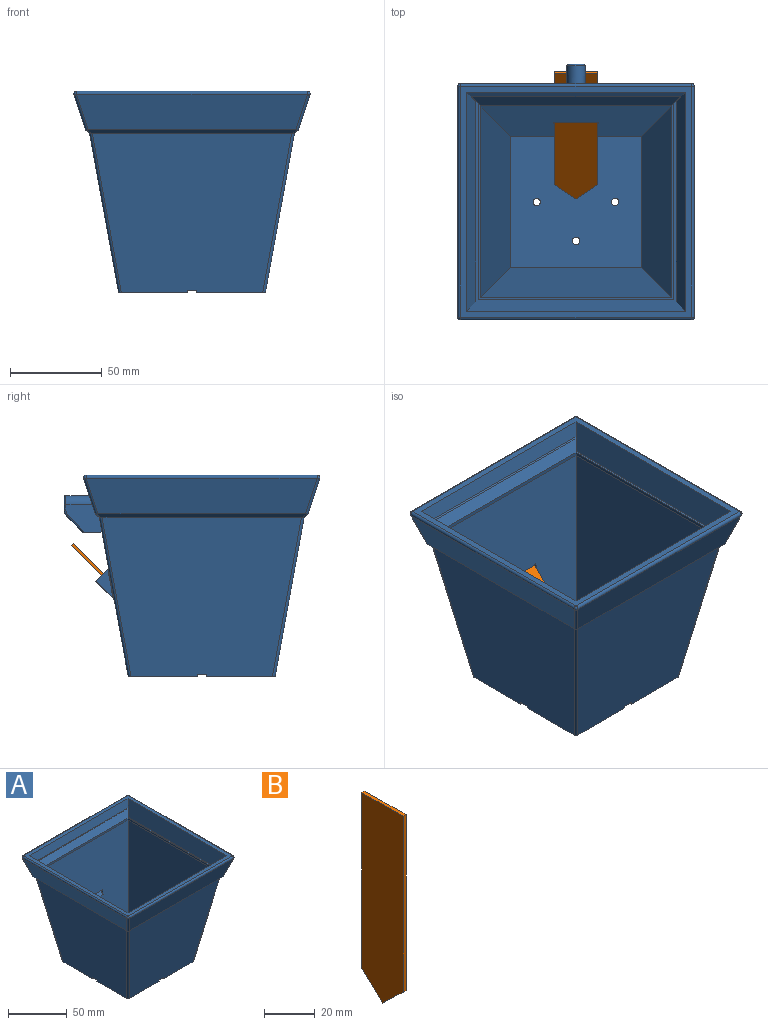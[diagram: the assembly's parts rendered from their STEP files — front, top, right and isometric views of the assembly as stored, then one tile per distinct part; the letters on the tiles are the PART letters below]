
ASSEMBLY  parts=2 mates=1
PART A: 106 faces, bbox 128.8x139.8x110.1 mm
  f0: plane 19.66x15mm, normal (1,0,0), area 207.3mm2, adj f2,f3,f19,f73,f74,f99,f100,f103
  f1: plane 19.66x15mm, normal (-1,0,0), area 207.3mm2, adj f2,f19,f47,f73,f74,f96,f97,f105
  f2: plane 108.7x87.05mm, normal (0,0.98,-0.18), area 7581.6mm2, adj f0,f1,f3,f8,f16,f44,f47,f49
  f3: plane 51.94x2.23mm, normal (0,0.64,-0.77), area 142.9mm2, adj f0,f2,f19,f53,f56,f60
  f4: plane 37.5x37.5mm, normal (0,0,-1), area 1405.8mm2, adj f5,f7,f11,f51,f72
  f5: plane 108.7x87.05mm, normal (0,-0.98,-0.18), area 8209.6mm2, adj f4,f10,f44,f46,f51,f66,f71,f72
  f6: plane 37.77x1.5mm, normal (0,1,0), area 56.5mm2, adj f10,f15,f44,f71
  f7: plane 37.77x1.5mm, normal (0,1,0), area 56.5mm2, adj f4,f11,f44,f72
  f8: plane 37.5x37.5mm, normal (0,0,-1), area 1405.8mm2, adj f2,f9,f15,f53,f69
  f9: plane 37.77x1.5mm, normal (0,-1,0), area 56.5mm2, adj f8,f15,f44,f69
  f10: plane 37.5x37.5mm, normal (0,0,-1), area 1405.8mm2, adj f5,f6,f15,f66,f71
  f11: plane 108.7x87.05mm, normal (-0.98,0,-0.18), area 8209.6mm2, adj f4,f7,f16,f43,f44,f48,f49,f51
  f12: plane 106.38x106.38mm, normal (0,0,1), area 316.1mm2, adj f27,f28,f30,f31,f32,f33,f39,f41
  f13: plane 119.46x7.5mm, normal (0,-0.95,0.31), area 924.4mm2, adj f21,f24,f25,f42
  f14: plane 113.86x6.55mm, normal (0,-0.95,0.31), area 770.8mm2, adj f22,f24,f25,f40
  f15: plane 108.7x87.05mm, normal (0.98,0,-0.18), area 8209.6mm2, adj f6,f8,f9,f10,f44,f45,f53,f66
  f16: plane 37.5x37.5mm, normal (0,0,-1), area 1405.8mm2, adj f2,f11,f43,f49,f70
  f17: plane 125.84x19.18mm, normal (0,-0.95,-0.31), area 2414.7mm2, adj f46,f57,f63,f67
  f18: plane 125.84x19.18mm, normal (0.95,0,-0.31), area 2414.7mm2, adj f45,f60,f64,f67
  f19: plane 125.84x19.18mm, normal (0,0.95,-0.31), area 2320.6mm2, adj f0,f1,f3,f47,f52,f59,f60,f73
  f20: plane 125.84x19.18mm, normal (-0.95,0,-0.31), area 2414.7mm2, adj f48,f52,f57,f58
  f21: plane 125.84x125.84mm, normal (0,0,1), area 1565mm2, adj f13,f23,f24,f25,f58,f59,f63,f64
  f22: plane 109.51x109.51mm, normal (0,0,1), area 675.3mm2, adj f14,f23,f24,f25,f29,f30,f31,f32
  f23: plane 119.46x15mm, normal (0,0.95,0.31), area 1809.4mm2, adj f21,f22,f24,f25
  f24: plane 119.46x15mm, normal (-0.95,0,0.31), area 1809.4mm2, adj f13,f14,f21,f22,f23,f41
  f25: plane 119.46x15mm, normal (0.95,0,0.31), area 1809.4mm2, adj f13,f14,f21,f22,f23,f39
  f26: plane 104.38x2mm, normal (0,-1,0), area 208.8mm2, adj f27,f33,f35,f42
  f27: plane 104.38x2mm, normal (-1,0,0), area 208.8mm2, adj f12,f26,f28,f38
  f28: plane 104.38x2mm, normal (0,1,0), area 208.8mm2, adj f12,f27,f33,f37
  f29: plane 106.38x2mm, normal (0,1,0), area 212.8mm2, adj f22,f30,f32,f40
  f30: plane 106.38x2mm, normal (-1,0,0), area 212.8mm2, adj f12,f22,f29,f31
  f31: plane 106.38x2mm, normal (0,-1,0), area 212.8mm2, adj f12,f22,f30,f32
  f32: plane 106.38x2mm, normal (1,0,0), area 212.8mm2, adj f12,f22,f29,f31
  f33: plane 104.38x2mm, normal (1,0,0), area 208.8mm2, adj f12,f26,f28,f36
  f34: plane 71.65x71.65mm, normal (0,0,1), area 5084.1mm2, adj f35,f36,f37,f38,f91,f92,f93,f94
  f35: plane 104.38x90mm, normal (0,-0.98,0.18), area 7942.5mm2, adj f26,f34,f36,f38,f80,f81,f82,f83
  f36: plane 104.38x90mm, normal (0.98,0,0.18), area 8051.5mm2, adj f33,f34,f35,f37
  f37: plane 104.38x90mm, normal (0,0.98,0.18), area 8051.5mm2, adj f28,f34,f36,f38
  f38: plane 104.38x90mm, normal (-0.98,0,0.18), area 8051.5mm2, adj f27,f34,f35,f37
  f39: plane 5.5x5.05mm, normal (-0.71,-0.71,0), area 5.4mm2, adj f12,f25,f40,f42
  f40: plane 113.86x4.55mm, normal (0,0.77,-0.63), area 648.5mm2, adj f14,f29,f39,f41
  f41: plane 5.5x5.05mm, normal (0.71,-0.71,0), area 5.4mm2, adj f12,f24,f40,f42
  f42: plane 114.49x5.5mm, normal (0,-0.74,0.68), area 817.3mm2, adj f13,f26,f39,f41
  f43: plane 37.77x1.5mm, normal (0,-1,0), area 56.5mm2, adj f11,f16,f44,f70
  f44: plane 80.55x80.55mm, normal (0,0,-1), area 730.2mm2, adj f2,f5,f6,f7,f9,f11,f15,f43
  f45: plane 113.89x2.23mm, normal (0.64,0,-0.77), area 313.9mm2, adj f15,f18,f53,f56,f60,f66,f67,f68
  f46: plane 113.89x2.23mm, normal (0,-0.64,-0.77), area 313.9mm2, adj f5,f17,f51,f54,f57,f66,f67,f68
  f47: plane 51.94x2.23mm, normal (0,0.64,-0.77), area 142.9mm2, adj f1,f2,f19,f49,f50,f52
  f48: plane 113.89x2.23mm, normal (-0.64,0,-0.77), area 313.9mm2, adj f11,f20,f49,f50,f51,f52,f54,f57
  f49: cylinder r=1.5mm len=87.17mm, axis (0.18,-0.18,-0.97), area 207.2mm2, adj f2,f11,f16,f47,f48,f50
  f50: cylinder r=1.5mm len=3.15mm, axis (-0.61,0.61,0.51), area 5mm2, adj f47,f48,f49,f52
  f51: cylinder r=1.5mm len=87.17mm, axis (-0.18,-0.18,0.97), area 207.2mm2, adj f4,f5,f11,f46,f48,f54
  f52: cylinder r=1.5mm len=19.36mm, axis (-0.3,0.3,0.91), area 46.7mm2, adj f19,f20,f47,f48,f50,f55
  f53: cylinder r=1.5mm len=87.17mm, axis (0.18,0.18,0.97), area 207.2mm2, adj f2,f3,f8,f15,f45,f56
  f54: cylinder r=1.5mm len=3.15mm, axis (-0.61,-0.61,0.51), area 5mm2, adj f46,f48,f51,f57
  f55: sphere r=1.5mm, area 4.9mm2, adj f52,f58,f59
  f56: cylinder r=1.5mm len=3.15mm, axis (-0.61,-0.61,-0.51), area 5mm2, adj f3,f45,f53,f60
  f57: cylinder r=1.5mm len=19.36mm, axis (-0.3,-0.3,0.91), area 46.7mm2, adj f17,f20,f46,f48,f54,f61
  f58: cylinder r=1.5mm len=125.84mm, axis (0,-1,0), area 357mm2, adj f20,f21,f55,f61
  f59: cylinder r=1.5mm len=125.84mm, axis (-1,0,0), area 357mm2, adj f19,f21,f55,f62
  f60: cylinder r=1.5mm len=19.36mm, axis (0.3,0.3,0.91), area 46.7mm2, adj f3,f18,f19,f45,f56,f62
  f61: sphere r=1.5mm, area 4.9mm2, adj f57,f58,f63
  f62: sphere r=1.5mm, area 4.9mm2, adj f59,f60,f64
  f63: cylinder r=1.5mm len=125.84mm, axis (1,0,0), area 357mm2, adj f17,f21,f61,f65
  f64: cylinder r=1.5mm len=125.84mm, axis (0,1,0), area 357mm2, adj f18,f21,f62,f65
  f65: sphere r=1.5mm, area 4.9mm2, adj f63,f64,f67
  f66: cylinder r=1.5mm len=87.17mm, axis (-0.18,0.18,-0.97), area 207.2mm2, adj f5,f10,f15,f45,f46,f68
  f67: cylinder r=1.5mm len=19.36mm, axis (0.3,-0.3,0.91), area 46.7mm2, adj f17,f18,f45,f46,f65,f68
  f68: cylinder r=1.5mm len=3.15mm, axis (-0.61,0.61,-0.51), area 5mm2, adj f45,f46,f66,f67
  f69: plane 37.77x1.5mm, normal (-1,0,0), area 56.5mm2, adj f2,f8,f9,f44
  f70: plane 37.77x1.5mm, normal (1,0,0), area 56.5mm2, adj f2,f16,f43,f44
  f71: plane 37.77x1.5mm, normal (-1,0,0), area 56.5mm2, adj f5,f6,f10,f44
  f72: plane 37.77x1.5mm, normal (1,0,0), area 56.5mm2, adj f4,f5,f7,f44
  f73: cylinder r=5mm len=14.36mm, axis (0,1,0), area 209mm2, adj f0,f1,f19,f98
  f74: plane 10.66x10mm, normal (0,0,-1), area 106mm2, adj f0,f1,f2,f95,f96,f100
  f75: plane 8x6.93mm, normal (0,1,0), area 36mm2, adj f97,f98,f99,f101,f104
  f76: plane 15.25x9.03mm, normal (-1,0,0), area 56.4mm2, adj f79,f84,f85
  f77: plane 29x10.04mm, normal (0,0.7,-0.71), area 409.6mm2, adj f79,f84,f87,f90
  f78: plane 15.25x9.03mm, normal (1,0,0), area 56.4mm2, adj f79,f86,f87
  f79: plane 31x7.11mm, normal (0,0.71,0.7), area 237.5mm2, adj f2,f76,f77,f78,f80,f81,f82,f83
  f80: plane 25x10mm, normal (0,0.7,-0.71), area 351.8mm2, adj f35,f79,f81,f82
  f81: plane 14.19x12.54mm, normal (1,0,0), area 39.6mm2, adj f35,f79,f80,f83
  f82: plane 14.19x12.54mm, normal (-1,0,0), area 39.6mm2, adj f35,f79,f80,f83
  f83: plane 25x12.54mm, normal (0,-0.7,0.71), area 441.1mm2, adj f35,f79,f81,f82
  f84: cylinder r=0.5mm len=10.39mm, axis (0,-0.71,-0.7), area 10.7mm2, adj f76,f77,f79,f88
  f85: cylinder r=0.5mm len=15.68mm, axis (0,0.18,0.98), area 12.3mm2, adj f2,f76,f79,f88
  f86: cylinder r=0.5mm len=15.68mm, axis (0,-0.18,-0.98), area 12.3mm2, adj f2,f78,f79,f89
  f87: cylinder r=0.5mm len=10.39mm, axis (0,0.71,0.7), area 10.7mm2, adj f77,f78,f79,f89
  f88: bspline ~1.72x1mm, area 1mm2, adj f2,f84,f85,f90
  f89: bspline ~1.72x1mm, area 1mm2, adj f2,f86,f87,f90
  f90: cylinder r=0.5mm len=29mm, axis (-1,0,0), area 8.9mm2, adj f2,f77,f88,f89
  f91: cylinder r=2mm len=4mm, axis (0,0,-1), area 44mm2, adj f34,f44
  f92: cylinder r=2mm len=4mm, axis (0,0,-1), area 44mm2, adj f34,f44
  f93: cylinder r=2mm len=4mm, axis (0,0,-1), area 44mm2, adj f34,f44
  f94: cylinder r=2mm len=4mm, axis (0,0,-1), area 44mm2, adj f34,f44
  f95: plane 8.54x8.54mm, normal (0,0.71,-0.71), area 96.6mm2, adj f74,f96,f100,f104
  f96: cylinder r=1mm len=9.95mm, axis (0,-0.71,-0.71), area 19.5mm2, adj f1,f74,f95,f105
  f97: cylinder r=1mm len=2.93mm, axis (0,0,-1), area 4.6mm2, adj f1,f75,f98,f105
  f98: torus R=4mm, axis (0,-1,0), area 22.9mm2, adj f73,f75,f97,f99
  f99: cylinder r=1mm len=2.93mm, axis (0,0,1), area 4.6mm2, adj f0,f75,f98,f103
  f100: cylinder r=1mm len=9.95mm, axis (0,0.71,0.71), area 19.5mm2, adj f0,f74,f95,f103
  f101: cylinder r=2mm len=10.5mm, axis (0,1,0), area 131.9mm2, adj f75,f102
  f102: plane 4x4mm, normal (0,1,0), area 12.6mm2, adj f101
  f103: torus R=4mm, axis (1,0,0), area 5.7mm2, adj f0,f99,f100,f104
  f104: cylinder r=5mm len=8mm, axis (1,0,0), area 31.4mm2, adj f75,f95,f103,f105
  f105: torus R=4mm, axis (-1,0,0), area 5.7mm2, adj f1,f96,f97,f104
PART B: 7 faces, bbox 1.7x23x96 mm
  f0: plane 11.5x11mm, normal (0,-0.69,-0.72), area 26.3mm2, adj f1,f4,f5,f6
  f1: plane 11.5x11mm, normal (0,0.69,-0.72), area 26.3mm2, adj f0,f2,f5,f6
  f2: plane 85x1.65mm, normal (0,1,0), area 140.2mm2, adj f1,f3,f5,f6
  f3: plane 23x1.65mm, normal (0,0,1), area 37.9mm2, adj f2,f4,f5,f6
  f4: plane 85x1.65mm, normal (0,-1,0), area 140.2mm2, adj f0,f3,f5,f6
  f5: plane 96x23mm, normal (1,0,0), area 2081.5mm2, adj f0,f1,f2,f3,f4
  f6: plane 96x23mm, normal (-1,0,0), area 2081.5mm2, adj f0,f1,f2,f3,f4
PLACE A t=(-9.12,7.01,-51.87)mm fixed
PLACE B rot(axis=(-0.36,0.36,0.86),98.5deg) t=(-9.12,8.68,-46.66)mm
MATE fastened B.f6 <-> A.f80  axis (0,-0.7,0.71) through (-9.12,44.72,-11)mm
